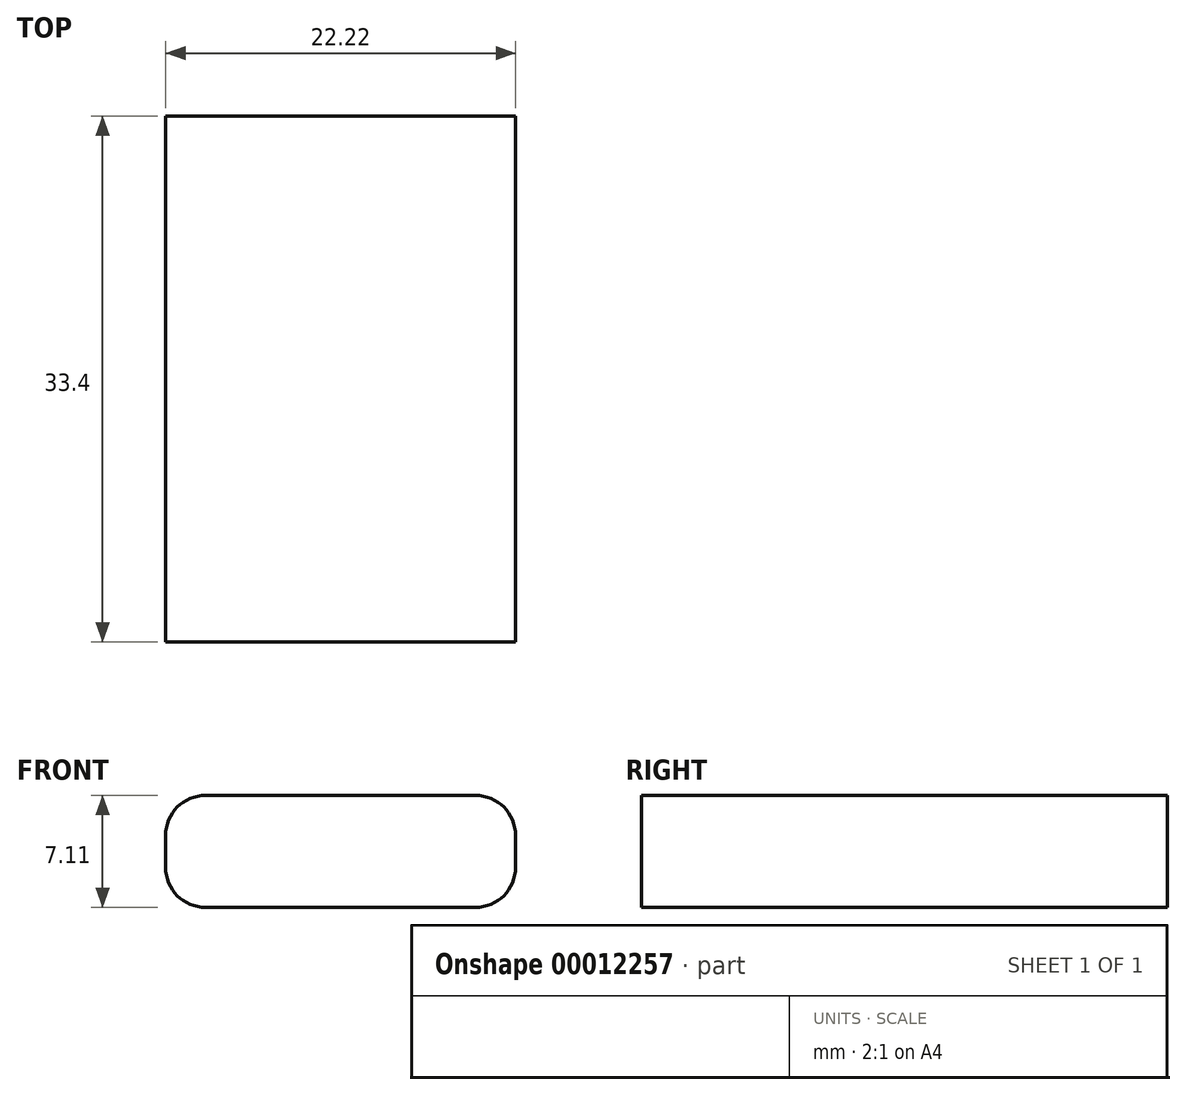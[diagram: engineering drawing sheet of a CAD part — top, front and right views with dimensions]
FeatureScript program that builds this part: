
annotation { "Feature Type Name" : "Feature", "Feature Type Description" : "" }
export const myFeature = defineFeature(function(context is Context, id is Id, definition is map)
    precondition{}
    {
        {
            var Q0;
            Q0=qCreatedBy(makeId("Top.planeOp"),FACE);
            var sketch = newSketch(context, id + "F0", { "sketchPlane" : qUnion([Q0])});
            skLineSegment(sketch, "E0.rect.bottom", {"start": v(11.11, 16.7) * mm, "end": v(-11.11, 16.7) * mm});
            skLineSegment(sketch, "E0.rect.top", {"start": v(11.11, -16.7) * mm, "end": v(-11.11, -16.7) * mm});
            skLineSegment(sketch, "E0.rect.left", {"start": v(11.11, 16.7) * mm, "end": v(11.11, -16.7) * mm});
            skLineSegment(sketch, "E0.rect.right", {"start": v(-11.11, 16.7) * mm, "end": v(-11.11, -16.7) * mm});
            skPoint(sketch, "E0.rect.middle", {"position": v(0, 0) * mm});
            skSolve(sketch);
        }
        {
            var Q0;
            Q0 = qSketchRegion(id + "F0", true);
            extrude(context, id + "F1", {"entities" : qUnion([Q0]), "depth" : 7.11 * mm});
        }
        {
            var Q0;
            Q0=makeQuery(id+"F1.opExtrude","CAP_EDGE",EDGE,{"disambiguationData":[OSD([sQuery(id+"F0.wireOp",EDGE,"E0.rect.right")])],"isStart":false});
            var Q1;
            Q1=makeQuery(id+"F1.opExtrude","CAP_EDGE",EDGE,{"disambiguationData":[OSD([sQuery(id+"F0.wireOp",EDGE,"E0.rect.left")])],"isStart":false});
            var Q2;
            Q2=makeQuery(id+"F1.opExtrude","CAP_EDGE",EDGE,{"disambiguationData":[OSD([sQuery(id+"F0.wireOp",EDGE,"E0.rect.left")])],"isStart":true});
            var Q3;
            Q3=makeQuery(id+"F1.opExtrude","CAP_EDGE",EDGE,{"disambiguationData":[OSD([sQuery(id+"F0.wireOp",EDGE,"E0.rect.right")])],"isStart":true});
            fillet(context, id + "F2", {"entities" : qUnion([Q0, Q1, Q2, Q3]), "radius" : 2.54 * mm, "tangentPropagation" : true, "allowEdgeOverflow" : false});
        }
    });
